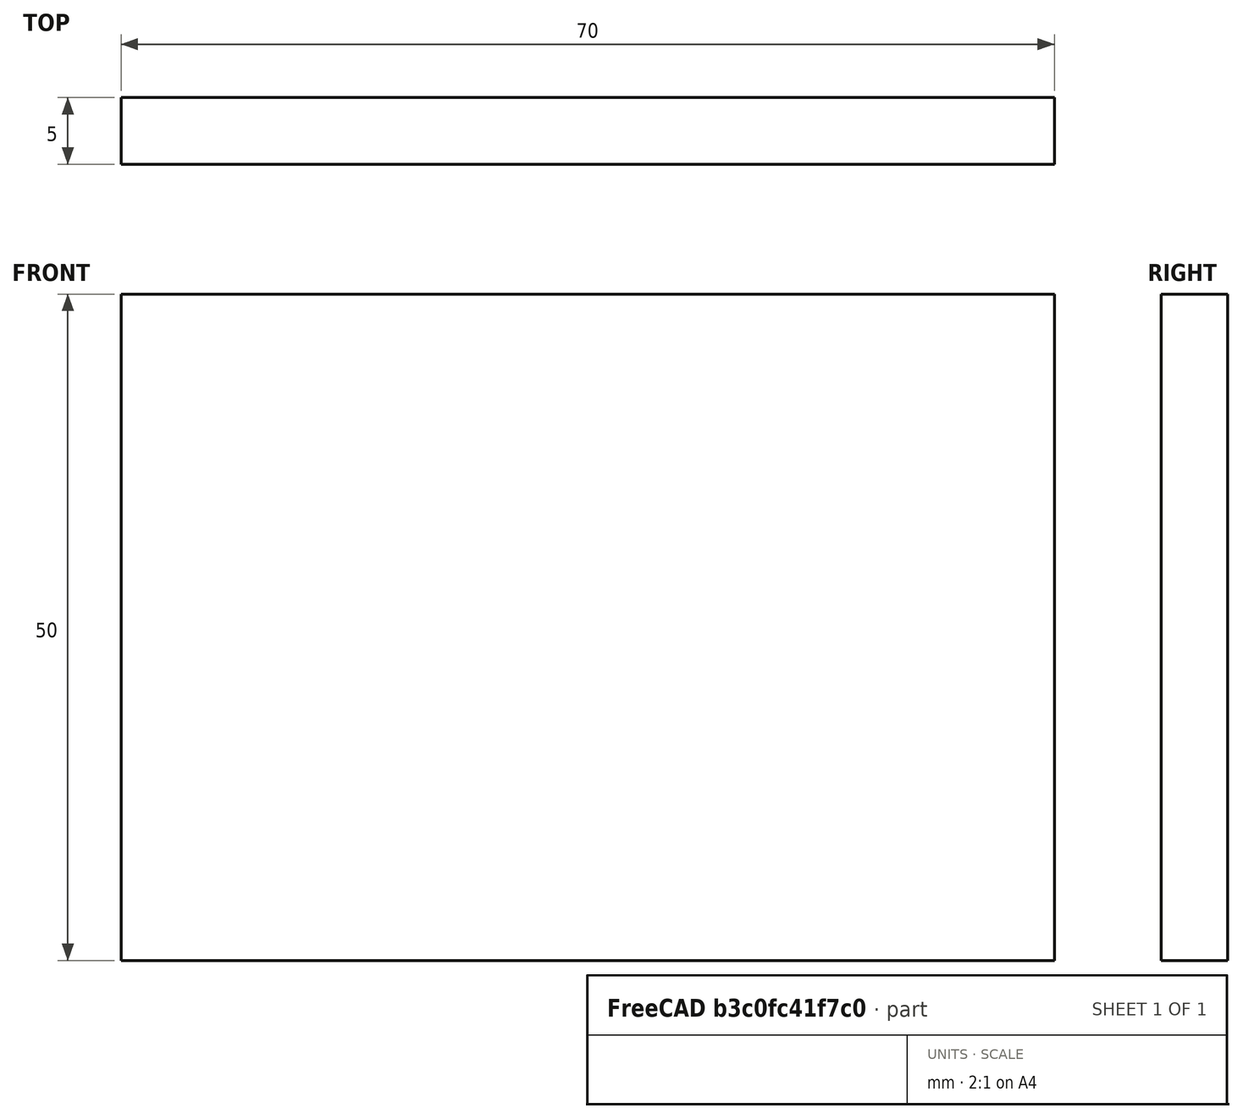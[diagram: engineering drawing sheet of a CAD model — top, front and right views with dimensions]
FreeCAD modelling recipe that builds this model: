
FCSTD DOCUMENT  (FreeCAD 0.15R4671 (Git))
Label: Flat Bar 70x5 EN10058 S235JR
License: All rights reserved
LicenseURL: http://en.wikipedia.org/wiki/All_rights_reserved
objects: Sketcher::SketchObject×1, Part::Extrusion×1
note: 2 computed .brp shape members not serialized (recipe doc carries the construction recipe); baked Part::Feature solids carry a one-line shape summary decoded from their .brp

FEATURE [Sketcher::SketchObject] Sketch
  sketch-geometry (4):
    g0: LineSegment StartX=-35 StartY=-2.5 StartZ=0 EndX=35 EndY=-2.5 EndZ=0
    g1: LineSegment StartX=35 StartY=-2.5 StartZ=0 EndX=35 EndY=2.5 EndZ=0
    g2: LineSegment StartX=35 StartY=2.5 StartZ=0 EndX=-35 EndY=2.5 EndZ=0
    g3: LineSegment StartX=-35 StartY=2.5 StartZ=0 EndX=-35 EndY=-2.5 EndZ=0
  constraints (12):
    c: Coincident(g0,g1)
    c: Coincident(g1,g2)
    c: Coincident(g2,g3)
    c: Coincident(g3,g0)
    c: Horizontal(g0)
    c: Horizontal(g2)
    c: Vertical(g1)
    c: Vertical(g3)
    c: Symmetric(g1,g2,g-2)
    c: Symmetric(g0,g1,g-1)
    c: DistanceY(g1) = 5
    c: DistanceX(g0) = 70
FEATURE [Part::Extrusion] Extrude  label="Flat Bar 70x5 EN10058 S235JR"
  Base = -> Sketch
  Dir = (0,0,50)
  Solid = true
